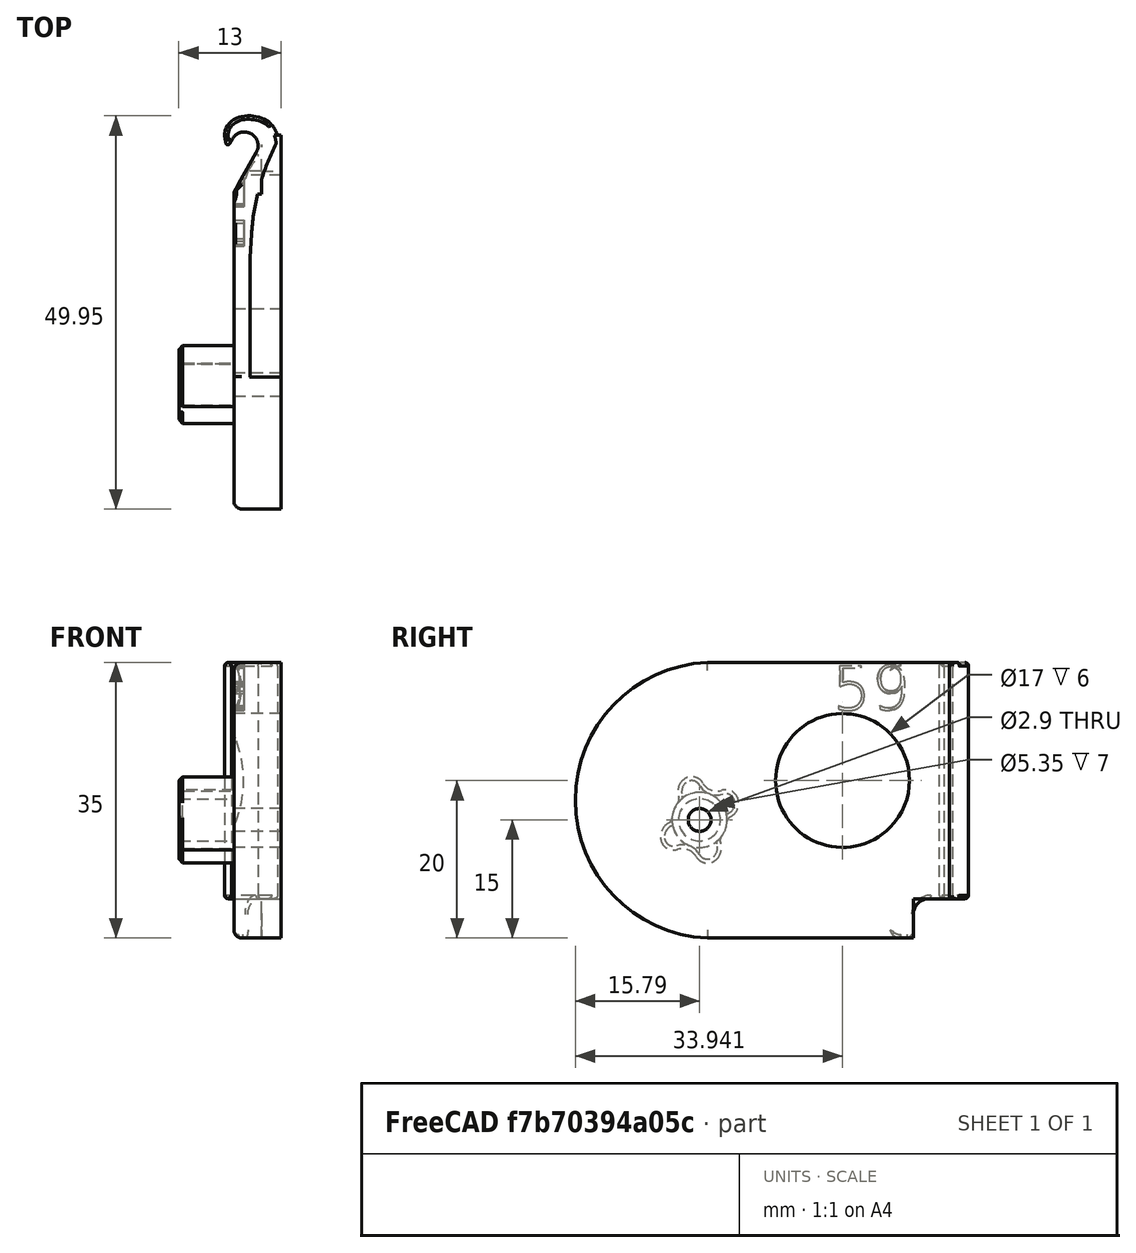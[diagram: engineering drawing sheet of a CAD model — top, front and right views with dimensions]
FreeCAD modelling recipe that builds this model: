
FCSTD DOCUMENT  (FreeCAD 0.18R)
Label: hinge-right-159deg-flat
License: All rights reserved
LicenseURL: http://en.wikipedia.org/wiki/All_rights_reserved
objects: App::FeaturePython×4, Part::FeaturePython×2, Part::Part2DObjectPython×1, Part::Extrusion×1, Part::Cut×1
note: 5 computed .brp shape members not serialized (recipe doc carries the construction recipe); baked Part::Feature solids carry a one-line shape summary decoded from their .brp

FEATURE [Part::FeaturePython] pillar_base_001  label="pillar-base_001"  # a2plus imported part (geometry in sourceFile) (typed FeaturePython)
  Placement = pos=(0.000608724,-57.1574,24.256) rot=(-1,0,0;0.802677rad)
  a2p_Version = V0.1
  fixedPosition = false
  objectType = a2pPart
  sourceFile = ./parts/pillar-base.fcstd
  subassemblyImport = false
  timeLastImport = 1.60452e+09
  updateColors = true
FEATURE [Part::Part2DObjectPython] ShapeString  # Draft 2D object (typed FeaturePython)
  FontFile = <path>
  Placement = pos=(1.61,10.5,29) rot=(0.57735,-0.57735,-0.57735;2.0944rad)
  Size = 6
  String = 59
  Tracking = 0
FEATURE [Part::Extrusion] Extrude
  Base = -> ShapeString
  Dir = (-1,0,0)
  DirMode = 2
  FaceMakerClass = Part::FaceMakerBullseye
  LengthFwd = 3.5
  LengthRev = 0
  Placement = pos=(0,0,0) rot=(0,0,1;3.14159rad)
  Solid = false
  Symmetric = false
FEATURE [Part::FeaturePython] bracket_right_flat_001  label="bracket-right-flat_001"  # a2plus imported part (geometry in sourceFile) (typed FeaturePython)
  Placement = pos=(0,0,0) rot=(0,0,1;3.14159rad)
  a2p_Version = V0.1
  fixedPosition = true
  objectType = a2pPart
  sourceFile = ./parts/bracket-right-flat.fcstd
  subassemblyImport = false
  timeLastImport = 1.60489e+09
  updateColors = true
FEATURE [App::FeaturePython] axisCoincident_001  label="axisCoincident_001__bracket-right-flat_001"  # a2plus constraint (typed FeaturePython)
  Object1 = pillar_base_001
  Object2 = bracket_right_flat_001
  ParentTreeObject = -> pillar_base_001
  SubElement1 = Face17
  SubElement2 = Face31
  Suppressed = false
  Type = axial
  directionConstraint = 1
  lockRotation = false
FEATURE [App::FeaturePython] axisCoincident_001_mirror  label="axisCoincident_001__pillar-base_001"  # a2plus constraint (typed FeaturePython)
  Object1 = pillar_base_001
  Object2 = bracket_right_flat_001
  ParentTreeObject = -> bracket_right_flat_001
  SubElement1 = Face17
  SubElement2 = Face31
  Suppressed = false
  Type = axial
  directionConstraint = 1
  lockRotation = false
FEATURE [App::FeaturePython] planeCoincident_001  label="planeCoincident_001__bracket-right-flat_001"  # a2plus constraint (typed FeaturePython)
  Object1 = pillar_base_001
  Object2 = bracket_right_flat_001
  ParentTreeObject = -> pillar_base_001
  SubElement1 = Face1
  SubElement2 = Face57
  Suppressed = false
  Type = plane
  directionConstraint = 1
  offset = 0
FEATURE [App::FeaturePython] planeCoincident_001_mirror  label="planeCoincident_001__pillar-base_001"  # a2plus constraint (typed FeaturePython)
  Object1 = pillar_base_001
  Object2 = bracket_right_flat_001
  ParentTreeObject = -> bracket_right_flat_001
  SubElement1 = Face1
  SubElement2 = Face57
  Suppressed = false
  Type = plane
  directionConstraint = 1
  offset = 0
FEATURE [Part::Cut] Cut
  Base = -> bracket_right_flat_001
  Tool = -> Extrude
note: 1 file-system path scrubbed to <path> (originals preserved in the JSON sidecar)
